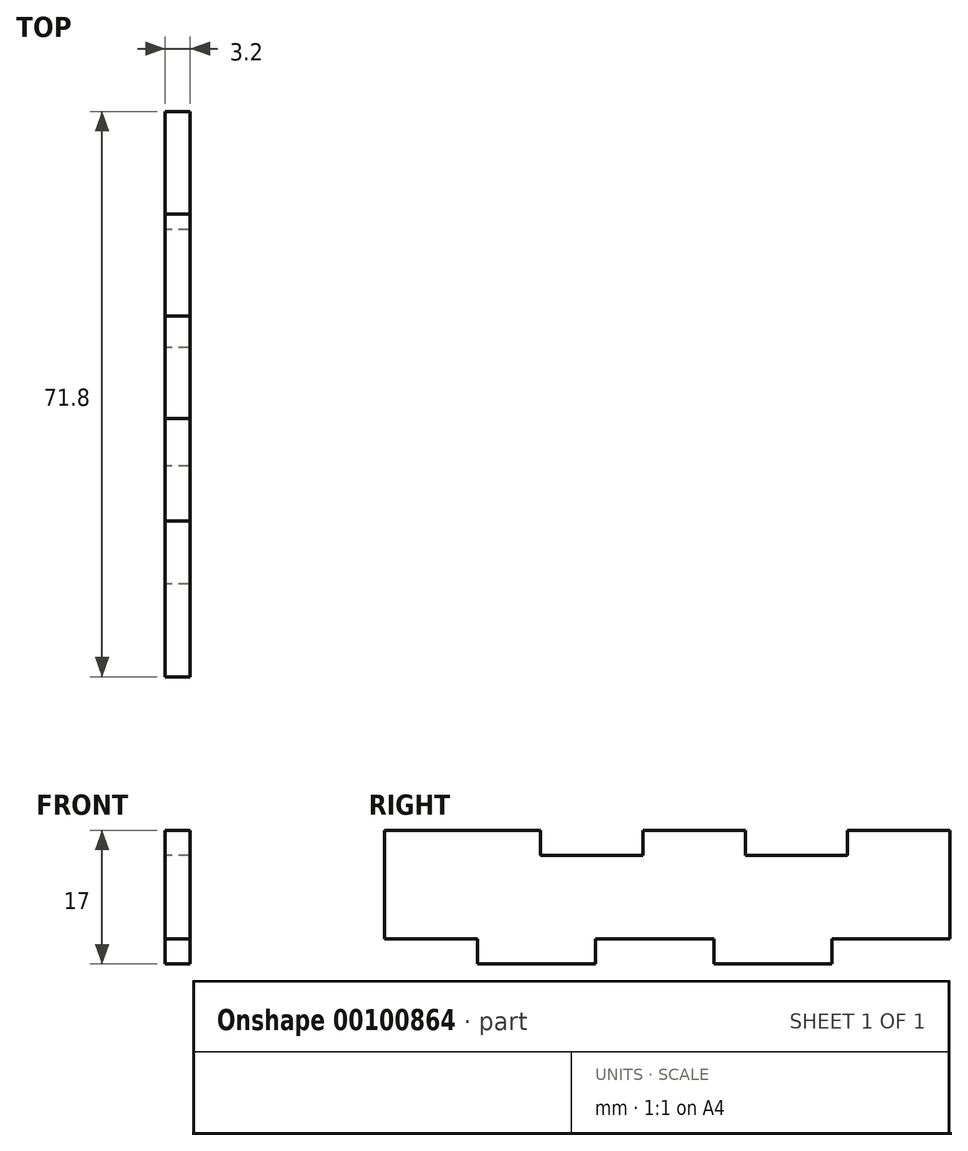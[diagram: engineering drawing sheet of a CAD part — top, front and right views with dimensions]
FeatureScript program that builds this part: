
annotation { "Feature Type Name" : "Feature", "Feature Type Description" : "" }
export const myFeature = defineFeature(function(context is Context, id is Id, definition is map)
    precondition{}
    {
        {
            var Q0;
            Q0=qCreatedBy(makeId("Right.planeOp"),FACE);
            var sketch = newSketch(context, id + "F0", { "sketchPlane" : qUnion([Q0])});
            skLineSegment(sketch, "E0.bottom", {"start": v(-34.3, 6) * mm, "end": v(-14.5, 6) * mm});
            skLineSegment(sketch, "E0.top", {"start": v(-22.5, -11) * mm, "end": v(-7.5, -11) * mm});
            skLineSegment(sketch, "E0.right", {"start": v(37.5, 6) * mm, "end": v(37.5, -2.8) * mm});
            skPoint(sketch, "E0.middle", {"position": v(0, 0) * mm});
            skLineSegment(sketch, "E1", {"start": v(22.5, -11) * mm, "end": v(7.5, -11) * mm});
            skLineSegment(sketch, "E2", {"start": v(7.5, -11) * mm, "end": v(7.5, -7.8) * mm});
            skLineSegment(sketch, "E3", {"start": v(7.5, -7.8) * mm, "end": v(-7.5, -7.8) * mm});
            skLineSegment(sketch, "E4", {"start": v(-7.5, -7.8) * mm, "end": v(-7.5, -11) * mm});
            skLineSegment(sketch, "E5", {"start": v(-7.5, -11) * mm, "end": v(-22.5, -11) * mm});
            skLineSegment(sketch, "E6", {"start": v(-22.5, -11) * mm, "end": v(-22.5, -7.8) * mm});
            skLineSegment(sketch, "E7", {"start": v(-22.5, -7.8) * mm, "end": v(-34.3, -7.8) * mm});
            skLineSegment(sketch, "E8", {"start": v(37.5, 6) * mm, "end": v(24.5, 6) * mm});
            skLineSegment(sketch, "E9", {"start": v(24.5, 6) * mm, "end": v(24.5, 2.8) * mm});
            skLineSegment(sketch, "E10", {"start": v(24.5, 2.8) * mm, "end": v(11.5, 2.8) * mm});
            skLineSegment(sketch, "E11", {"start": v(11.5, 2.8) * mm, "end": v(11.5, 6) * mm});
            skLineSegment(sketch, "E12", {"start": v(6.5, 6) * mm, "end": v(3.5, 6) * mm});
            skLineSegment(sketch, "E13", {"start": v(-1.5, 6) * mm, "end": v(-1.5, 2.8) * mm});
            skLineSegment(sketch, "E14", {"start": v(-1.5, 2.8) * mm, "end": v(-14.5, 2.8) * mm});
            skLineSegment(sketch, "E15", {"start": v(-14.5, 2.8) * mm, "end": v(-14.5, 6) * mm});
            skLineSegment(sketch, "E16", {"start": v(-14.5, 6) * mm, "end": v(-34.3, 6) * mm});
            skLineSegment(sketch, "E17", {"start": v(-34.3, -7.8) * mm, "end": v(-34.3, -5.9) * mm});
            skLineSegment(sketch, "E18", {"start": v(-34.3, -0.9) * mm, "end": v(-34.3, 6) * mm});
            skLineSegment(sketch, "E19.trimOffspring", {"start": v(7.5, -11) * mm, "end": v(22.5, -11) * mm});
            skLineSegment(sketch, "E20.trimOffspring", {"start": v(24.5, 6) * mm, "end": v(37.5, 6) * mm});
            skLineSegment(sketch, "E21", {"start": v(-22.5, -11) * mm, "end": v(-49.63, -11) * mm, "construction": true});
            skLineSegment(sketch, "E22", {"start": v(11.5, 6) * mm, "end": v(-1.5, 6) * mm});
            skLineSegment(sketch, "E23", {"start": v(22.5, -11) * mm, "end": v(22.5, -7.8) * mm});
            skLineSegment(sketch, "E24", {"start": v(22.5, -7.8) * mm, "end": v(37.5, -7.8) * mm});
            skLineSegment(sketch, "E25", {"start": v(37.5, -7.8) * mm, "end": v(37.5, -2.8) * mm});
            skLineSegment(sketch, "E26", {"start": v(-34.3, -5.9) * mm, "end": v(-34.3, -0.9) * mm});
            skSolve(sketch);
        }
        {
            var Q0;
            Q0=makeQuery(id+"F0.imprint","IMPRINT",FACE,{"disambiguationData":[TD([[makeQuery(id+"F0.imprint","IMPRINT",EDGE,{"derivedFrom":sQuery(id+"F0.wireOp",EDGE,"E0.right")}),-1.0]])]});
            extrude(context, id + "F1", {"entities" : qUnion([Q0]), "endBound" : BoundingType.SYMMETRIC, "depth" : 3.2 * mm});
        }
    });
